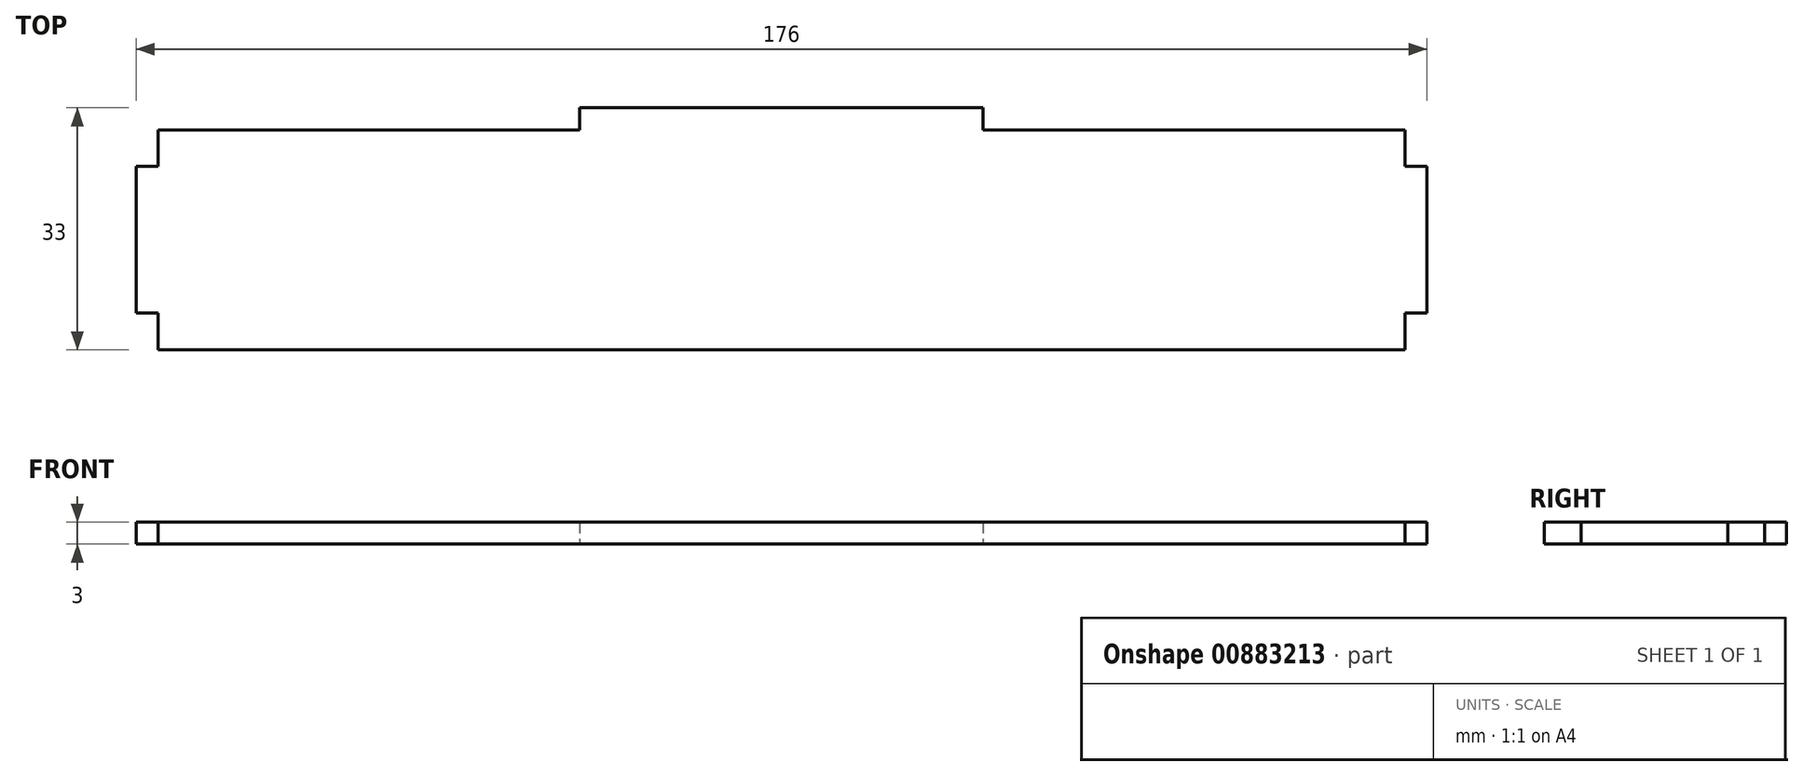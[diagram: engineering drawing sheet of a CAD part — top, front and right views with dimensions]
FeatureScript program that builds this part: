
annotation { "Feature Type Name" : "Feature", "Feature Type Description" : "" }
export const myFeature = defineFeature(function(context is Context, id is Id, definition is map)
    precondition{}
    {
        {
            var Q0;
            Q0=qCreatedBy(makeId("Top.planeOp"),FACE);
            var sketch = newSketch(context, id + "F0", { "sketchPlane" : qUnion([Q0])});
            skLineSegment(sketch, "E0.bottom", {"start": v(85, 15) * mm, "end": v(-85, 15) * mm});
            skLineSegment(sketch, "E0.top", {"start": v(85, -15) * mm, "end": v(-85, -15) * mm});
            skLineSegment(sketch, "E0.left", {"start": v(85, 15) * mm, "end": v(85, -15) * mm});
            skLineSegment(sketch, "E0.right", {"start": v(-85, 15) * mm, "end": v(-85, -15) * mm});
            skPoint(sketch, "E0.middle", {"position": v(0, 0) * mm});
            skLineSegment(sketch, "E1", {"start": v(85, 10) * mm, "end": v(88, 10) * mm});
            skLineSegment(sketch, "E2", {"start": v(88, 10) * mm, "end": v(88, -10) * mm});
            skLineSegment(sketch, "E3", {"start": v(88, -10) * mm, "end": v(85, -10) * mm});
            skLineSegment(sketch, "E4.MirrorCS", {"start": v(-85, 10) * mm, "end": v(-88, 10) * mm});
            skLineSegment(sketch, "E5.MirrorCS", {"start": v(-88, -10) * mm, "end": v(-85, -10) * mm});
            skLineSegment(sketch, "E6.MirrorCS", {"start": v(-88, 10) * mm, "end": v(-88, -10) * mm});
            skLineSegment(sketch, "E7", {"start": v(-27.5, 15) * mm, "end": v(-27.5, 18) * mm});
            skLineSegment(sketch, "E8", {"start": v(-27.5, 18) * mm, "end": v(27.5, 18) * mm});
            skLineSegment(sketch, "E9", {"start": v(27.5, 18) * mm, "end": v(27.5, 15) * mm});
            skSolve(sketch);
        }
        {
            var Q0;
            Q0 = qSketchRegion(id + "F0", true);
            extrude(context, id + "F1", {"entities" : qUnion([Q0]), "depth" : 3 * mm, "offsetDistance" : 25 * mm});
        }
    });
